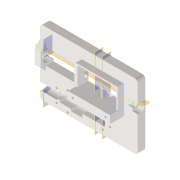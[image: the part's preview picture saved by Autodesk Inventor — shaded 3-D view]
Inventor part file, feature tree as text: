
AUTODESK INVENTOR PART (.ipt)
format: ipt  version: 2022 (Build 260153000, 153)  size: 443,904 bytes
history: native  units: mm
features: sketch x20, extrude x19, reference x11, other x10, plane x8, projected_geometry x7, fillet x2, chamfer x1, mirror x1, hole x1
ambient origin geometry x8: Origin, YZ Plane, XZ Plane, XY Plane, X Axis, Y Axis, Z Axis, Center Point
bodies: Solid1 (feature_tree)
feature tree (80):
  extrude  "Extrusion1"  Depth=10.0mm
  fillet  "Fillet1"  Radius=10.0mm
  extrude  "Extrusion2"  Depth=51.0mm
  extrude  "Extrusion3"  Depth=20.0mm
  plane  "Work Plane1"
  plane  "Work Plane2"
  chamfer  "Chamfer1"  [1 undecoded]
  extrude  "Extrusion4"  Depth=10.0mm
  extrude  "Extrusion5"  Depth=8.0mm
  extrude  "Extrusion6"  Depth=4.0mm TaperAngle=0.0deg
  plane  "Work Plane3"
  extrude  "Extrusion12"  Depth=20.0mm TaperAngle=0.0deg
  extrude  "Extrusion13"  Depth=10.0mm
  mirror  "Mirror1"
  plane  "Work Plane4"
  plane  "Work Plane5"
  extrude  "Extrusion21"  Depth=2.0mm
  extrude  "Extrusion22"  Depth=30.0mm
  plane  "Arbeitsebene7"
  extrude  "Extrusion27"  Depth=7.0mm
  extrude  "Extrusion28"  Depth=10.0mm
  extrude  "Extrusion29"  Depth=6.0mm
  fillet  "Rundung6"  Radius=6.0mm
  sketch  "Skizze32"  dims[d61=30.0mm d62=-0.523599mm d63=12.0mm]
  plane  "Arbeitsebene8"
  extrude  "Extrusion30"  TaperAngle=0.0deg  [1 undecoded]
  extrude  "Extrusion31"  Depth=40.0mm TaperAngle=0.0deg
  extrude  "Extrusion32"  Depth=0.5mm
  extrude  "Extrusion33"  Depth=1.0mm TaperAngle=0.0deg
  sketch  "Skizze36"  dims[d108=6.0mm d109=0.0mm d110=0.0mm]
  plane  "Arbeitsebene9"
  extrude  "Extrusion34"  Depth=8.0mm
  extrude  "Extrusion35"  TaperAngle=45.0deg  [1 undecoded]
  hole  "Bohrung2"  [1 undecoded]
  sketch  "Sketch1"  dims[d0=127.8mm d1=85.5mm d2=10.0mm d3=0.0mm]
  sketch  "Sketch2"  dims[d4=4.0mm d5=51.0mm]
  projected_geometry  "Projected Loop1"
  sketch  "Sketch3"  dims[d6=25.0mm d7=20.0mm]
  projected_geometry  "Projected Loop2"
  sketch  "Sketch4"  dims[d8=15.0mm]
  projected_geometry  "Projected Loop3"
  sketch  "Sketch5"  dims[d9=6.0mm]
  sketch  "Sketch6"  dims[d10=0.0mm]
  reference  "Reference2"
  sketch  "Sketch12"  dims[d11=1.5mm d12=0.0mm d13=0.0mm]
  reference  "Reference4"
  sketch  "Sketch13"  dims[d14=4.0mm d15=2.0mm d16=45.0deg d17=10.0mm]
  sketch  "Sketch22"  dims[d18=8.0mm d19=0.0mm d20=1.9mm]
  projected_geometry  "Projected Loop8"
  sketch  "Sketch23"  dims[d21=4.0mm d22=5.0mm d23=0.0mm]
  projected_geometry  "Projected Loop9"
  reference  "Reference11"
  sketch  "Skizze28"  dims[d27=20.0mm d28=18.0mm d29=0.0mm]
  sketch  "Skizze29"  dims[d38=10.0mm d52=2.0mm]
  reference  "Referenz13"
  sketch  "Skizze30"  dims[d53=2.0mm d54=2.0mm]
  reference  "Referenz14"
  reference  "Referenz16"
  sketch  "Skizze33"  dims[d64=7.0mm d65=0.0mm d100=7.0mm]
  reference  "Referenz17"
  sketch  "Skizze34"  dims[d101=10.0mm d102=0.0mm d103=11.8mm]
  reference  "Referenz18"
  sketch  "Skizze35"  dims[d105=2.8mm d106=2.8mm d107=6.0mm]
  projected_geometry  "Projizierte Kontur15"
  reference  "Referenz19"
  reference  "Referenz20"
  sketch  "Skizze37"  dims[d142=0.5mm d143=40.0mm d144=0.0mm]
  reference  "Referenz21"
  sketch  "Skizze38"  dims[d145=8.0mm d146=0.0mm d147=0.5mm d148=1.0mm d149=0.0mm d150=2.0mm d151=45.0deg d152=45.0deg d153=8.0mm d154=0.0mm d155=7.0mm d156=3.0mm d157=0.0mm d158=30.0mm d159=0.0mm d160=17.0mm d161=15.0mm d162=0.0mm d163=0.5mm d164=15.0mm d165=0.0mm d166=8.0mm d167=10.0mm d168=0.0mm d169=2.8mm d170=6.0mm d171=4.0mm d172=2.0mm d173=90.0deg d174=8.0mm d175=20.594885mm]
  projected_geometry  "Projizierte Kontur16"
  other  "<userpath>\Documents\GitHub\Guinardia\INVENTOR\Assembly_Guinardia_V1.iam"
  other  "Assembly_Guinardia_V1.iam"
  other  "00_CCTV_lens_M12_25mm_5mp:1"
  other  "00_PipetteTip200ul-1:2"
  other  "00_NEMA8:1"
  other  "00_SM05FC2-Step:1"
  other  "00_CCTV_lens_M12_25mm_5mp:2"
  other  "00_HuaweiP30_Telelens_prismonly:1"
  other  "<userpath>\Documents\Inventor\Guinardia\INVENTOR\Assembly_Guinardia_V0.iam"
  other  "Assembly_Guinardia_V0.iam"
note: 4 required parameter values undecoded (feature->parameter linkage not recoverable at this tier; creation-order binding heuristic only, values carry confidence <= 0.55)
